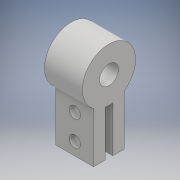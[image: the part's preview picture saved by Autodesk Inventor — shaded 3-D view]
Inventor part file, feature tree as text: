
AUTODESK INVENTOR PART (.ipt)
format: ipt  version: 2017 (Build 210142000, 142)  size: 130,048 bytes
history: native  units: mm
features: extrude x2, sketch x2
ambient origin geometry x8: Origin, YZ Plane, XZ Plane, XY Plane, X Axis, Y Axis, Z Axis, Center Point
bodies: Solid1 (feature_tree)
feature tree (4):
  extrude  "Extrusion1"  Depth=2.5mm
  extrude  "Extrusion2"  Depth=5.0mm
  sketch  "Sketch1"  dims[d0=7.0mm d1=2.5mm]
  sketch  "Sketch2"  dims[d2=0.5mm d3=6.0mm d4=5.0mm d5=0.0mm d6=1.5mm d7=1.5mm d8=5.0mm d9=0.0mm]
